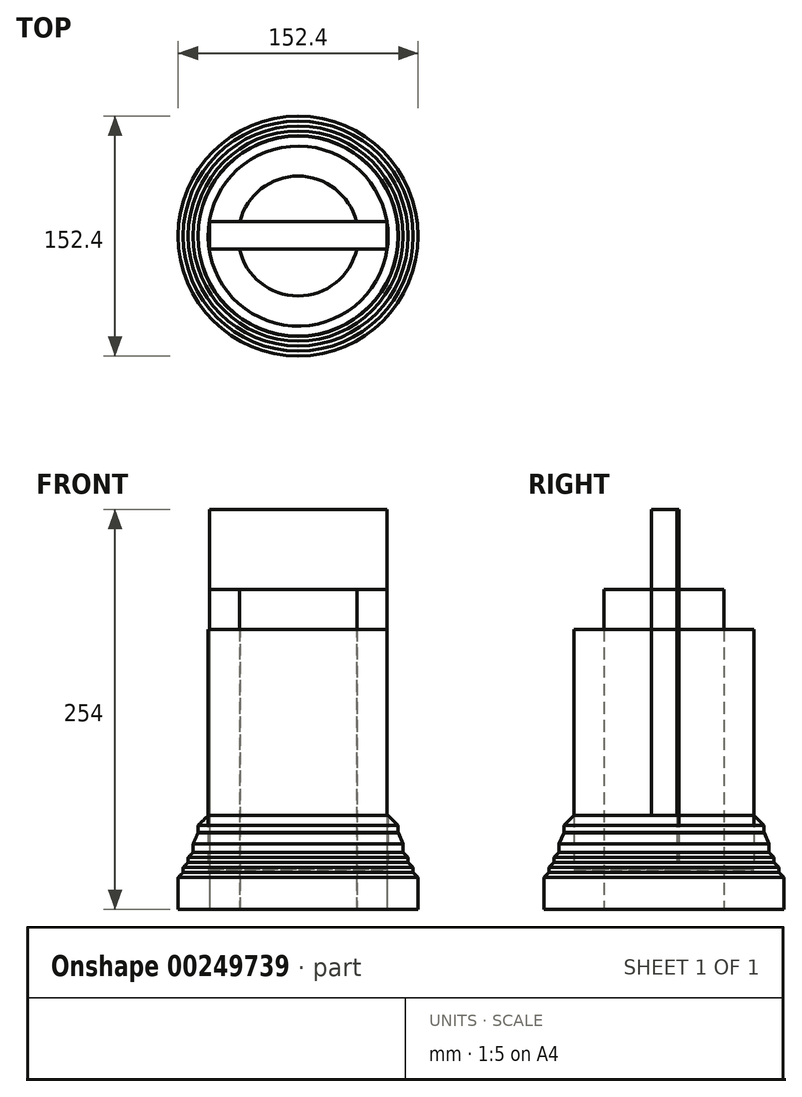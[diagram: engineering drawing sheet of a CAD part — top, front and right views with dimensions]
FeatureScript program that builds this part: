
annotation { "Feature Type Name" : "Feature", "Feature Type Description" : "" }
export const myFeature = defineFeature(function(context is Context, id is Id, definition is map)
    precondition{}
    {
        {
            var Q0;
            Q0=qCreatedBy(makeId("Top.planeOp"),FACE);
            var sketch = newSketch(context, id + "F0", { "sketchPlane" : qUnion([Q0])});
            skCircle(sketch, "E0", {"center": v(0, 0) * mm, "radius": 76.2 * mm});
            skCircle(sketch, "E1", {"center": v(0, 0) * mm, "radius": 57.15 * mm});
            skCircle(sketch, "E2", {"center": v(0, 0) * mm, "radius": 38.1 * mm});
            skLineSegment(sketch, "E3.bottom", {"start": v(-56.38, 9.32) * mm, "end": v(56.57, 9.32) * mm});
            skLineSegment(sketch, "E3.top", {"start": v(-56.38, -8.13) * mm, "end": v(56.57, -8.13) * mm});
            skLineSegment(sketch, "E3.left", {"start": v(-56.38, 9.32) * mm, "end": v(-56.38, -8.13) * mm});
            skLineSegment(sketch, "E3.right", {"start": v(56.57, 9.32) * mm, "end": v(56.57, -8.13) * mm});
            skCircle(sketch, "E4", {"center": v(0, 0) * mm, "radius": 73.03 * mm});
            skCircle(sketch, "E5", {"center": v(0, 0) * mm, "radius": 69.85 * mm});
            skCircle(sketch, "E6", {"center": v(0, 0) * mm, "radius": 66.68 * mm});
            skCircle(sketch, "E7", {"center": v(0, 0) * mm, "radius": 63.5 * mm});
            skSolve(sketch);
        }
        {
            var Q0;
            {var subQ0=sQuery(id+"F0.wireOp",EDGE,"E3.top");var subQ1=sQuery(id+"F0.wireOp",EDGE,"E2");var subQ2=makeQuery(id+"F0.imprint","INTERSECT",VERTEX,{"disambiguationData":[OD(0.0)],"derivedFrom":[subQ1,subQ0]});Q0=makeQuery(id+"F0.imprint","IMPRINT",FACE,{"disambiguationData":[TD([[makeQuery(id+"F0.imprint","IMPRINT",EDGE,{"disambiguationData":[TD([[subQ2,-1.0]])],"derivedFrom":subQ1}),1.0]])]});}
            var Q1;
            Q1=makeQuery(id+"F0.imprint","IMPRINT",FACE,{"disambiguationData":[TD([[makeQuery(id+"F0.imprint","IMPRINT",EDGE,{"derivedFrom":sQuery(id+"F0.wireOp",EDGE,"E0")}),1.0]])]});
            var Q2;
            {var subQ0=sQuery(id+"F0.wireOp",EDGE,"E3.bottom");var subQ1=sQuery(id+"F0.wireOp",EDGE,"E2");var subQ2=makeQuery(id+"F0.imprint","INTERSECT",VERTEX,{"disambiguationData":[OD(0.0)],"derivedFrom":[subQ1,subQ0]});Q2=makeQuery(id+"F0.imprint","IMPRINT",FACE,{"disambiguationData":[TD([[makeQuery(id+"F0.imprint","IMPRINT",EDGE,{"disambiguationData":[TD([[subQ2,-1.0]])],"derivedFrom":subQ1}),1.0]])]});}
            var Q3;
            Q3=makeQuery(id+"F0.imprint","IMPRINT",FACE,{"disambiguationData":[TD([[makeQuery(id+"F0.imprint","IMPRINT",EDGE,{"derivedFrom":sQuery(id+"F0.wireOp",EDGE,"E7")}),1.0]])]});
            var Q4;
            {var subQ5=sQuery(id+"F0.wireOp",EDGE,"E3.left");Q4=makeQuery(id+"F0.imprint","IMPRINT",FACE,{"disambiguationData":[TD([[makeQuery(id+"F0.imprint","IMPRINT",EDGE,{"derivedFrom":subQ5}),-1.0]])]});}
            var Q5;
            {var subQ0=sQuery(id+"F0.wireOp",EDGE,"E3.bottom");var subQ4=sQuery(id+"F0.wireOp",EDGE,"E2");var subQ5=makeQuery(id+"F0.imprint","INTERSECT",VERTEX,{"disambiguationData":[OD(0.0)],"derivedFrom":[subQ4,subQ0]});Q5=makeQuery(id+"F0.imprint","IMPRINT",FACE,{"disambiguationData":[TD([[makeQuery(id+"F0.imprint","IMPRINT",EDGE,{"disambiguationData":[TD([[subQ5,1.0]])],"derivedFrom":subQ4}),-1.0]])]});}
            var Q6;
            {var subQ5=sQuery(id+"F0.wireOp",EDGE,"E3.left");Q6=makeQuery(id+"F0.imprint","IMPRINT",FACE,{"disambiguationData":[TD([[makeQuery(id+"F0.imprint","IMPRINT",EDGE,{"derivedFrom":subQ5}),1.0]])]});}
            var Q7;
            Q7=makeQuery(id+"F0.imprint","IMPRINT",FACE,{"disambiguationData":[TD([[makeQuery(id+"F0.imprint","IMPRINT",EDGE,{"derivedFrom":sQuery(id+"F0.wireOp",EDGE,"E6")}),1.0]])]});
            var Q8;
            Q8=makeQuery(id+"F0.imprint","IMPRINT",FACE,{"disambiguationData":[TD([[makeQuery(id+"F0.imprint","IMPRINT",EDGE,{"derivedFrom":sQuery(id+"F0.wireOp",EDGE,"E5")}),1.0]])]});
            var Q9;
            {var subQ0=sQuery(id+"F0.wireOp",EDGE,"E3.bottom");var subQ1=sQuery(id+"F0.wireOp",EDGE,"E2");var subQ2=makeQuery(id+"F0.imprint","INTERSECT",VERTEX,{"disambiguationData":[OD(0.0)],"derivedFrom":[subQ1,subQ0]});Q9=makeQuery(id+"F0.imprint","IMPRINT",FACE,{"disambiguationData":[TD([[makeQuery(id+"F0.imprint","IMPRINT",EDGE,{"disambiguationData":[TD([[subQ2,1.0]])],"derivedFrom":subQ1}),1.0]])]});}
            var Q10;
            Q10=makeQuery(id+"F0.imprint","IMPRINT",FACE,{"disambiguationData":[TD([[makeQuery(id+"F0.imprint","IMPRINT",EDGE,{"derivedFrom":sQuery(id+"F0.wireOp",EDGE,"E4")}),1.0]])]});
            var Q11;
            {var subQ2=sQuery(id+"F0.wireOp",EDGE,"E1");var subQ6=sQuery(id+"F0.wireOp",EDGE,"E3.bottom");var subQ7=makeQuery(id+"F0.imprint","INTERSECT",VERTEX,{"derivedFrom":[subQ2,subQ6]});Q11=makeQuery(id+"F0.imprint","IMPRINT",FACE,{"disambiguationData":[TD([[makeQuery(id+"F0.imprint","IMPRINT",EDGE,{"disambiguationData":[TD([[subQ7,1.0]])],"derivedFrom":subQ2}),1.0]])]});}
            var Q12;
            {var subQ0=sQuery(id+"F0.wireOp",EDGE,"E3.right");var subQ1=sQuery(id+"F0.wireOp",EDGE,"E1");var subQ3=makeQuery(id+"F0.imprint","INTERSECT",VERTEX,{"derivedFrom":[subQ1,subQ0]});Q12=makeQuery(id+"F0.imprint","IMPRINT",FACE,{"disambiguationData":[TD([[makeQuery(id+"F0.imprint","IMPRINT",EDGE,{"disambiguationData":[TD([[subQ3,1.0]])],"derivedFrom":subQ1}),1.0]])]});}
            var Q13;
            {var subQ0=sQuery(id+"F0.wireOp",EDGE,"E3.bottom");var subQ1=sQuery(id+"F0.wireOp",EDGE,"E1");var subQ2=makeQuery(id+"F0.imprint","INTERSECT",VERTEX,{"derivedFrom":[subQ1,subQ0]});Q13=makeQuery(id+"F0.imprint","IMPRINT",FACE,{"disambiguationData":[TD([[makeQuery(id+"F0.imprint","IMPRINT",EDGE,{"disambiguationData":[TD([[subQ2,1.0]])],"derivedFrom":subQ1}),-1.0]])]});}
            extrude(context, id + "F1", {"entities" : qUnion([Q0, Q1, Q2, Q3, Q4, Q5, Q6, Q7, Q8, Q9, Q10, Q11, Q12, Q13]), "depth" : 25.4 * mm});
        }
        {
            var Q0;
            Q0=makeQuery(id+"F0.imprint","IMPRINT",FACE,{"disambiguationData":[TD([[makeQuery(id+"F0.imprint","IMPRINT",EDGE,{"derivedFrom":sQuery(id+"F0.wireOp",EDGE,"E4")}),1.0]])]});
            extrude(context, id + "F2", {"entities" : qUnion([Q0]), "operationType" : NewBodyOperationType.ADD, "depth" : 31.75 * mm});
        }
        {
            var Q0;
            Q0=makeQuery(id+"F0.imprint","IMPRINT",FACE,{"disambiguationData":[TD([[makeQuery(id+"F0.imprint","IMPRINT",EDGE,{"derivedFrom":sQuery(id+"F0.wireOp",EDGE,"E5")}),1.0]])]});
            extrude(context, id + "F3", {"entities" : qUnion([Q0]), "operationType" : NewBodyOperationType.ADD, "depth" : 38.1 * mm});
        }
        {
            var Q0;
            Q0=makeQuery(id+"F0.imprint","IMPRINT",FACE,{"disambiguationData":[TD([[makeQuery(id+"F0.imprint","IMPRINT",EDGE,{"derivedFrom":sQuery(id+"F0.wireOp",EDGE,"E6")}),1.0]])]});
            extrude(context, id + "F4", {"entities" : qUnion([Q0]), "operationType" : NewBodyOperationType.ADD, "depth" : 50.8 * mm});
        }
        {
            var Q0;
            Q0=makeQuery(id+"F0.imprint","IMPRINT",FACE,{"disambiguationData":[TD([[makeQuery(id+"F0.imprint","IMPRINT",EDGE,{"derivedFrom":sQuery(id+"F0.wireOp",EDGE,"E7")}),1.0]])]});
            extrude(context, id + "F5", {"entities" : qUnion([Q0]), "operationType" : NewBodyOperationType.ADD, "depth" : 63.5 * mm});
        }
        {
            var Q0;
            {var subQ0=sQuery(id+"F0.wireOp",EDGE,"E3.bottom");var subQ4=sQuery(id+"F0.wireOp",EDGE,"E2");var subQ5=makeQuery(id+"F0.imprint","INTERSECT",VERTEX,{"disambiguationData":[OD(0.0)],"derivedFrom":[subQ4,subQ0]});Q0=makeQuery(id+"F0.imprint","IMPRINT",FACE,{"disambiguationData":[TD([[makeQuery(id+"F0.imprint","IMPRINT",EDGE,{"disambiguationData":[TD([[subQ5,1.0]])],"derivedFrom":subQ4}),-1.0]])]});}
            var Q1;
            {var subQ2=sQuery(id+"F0.wireOp",EDGE,"E1");var subQ6=sQuery(id+"F0.wireOp",EDGE,"E3.bottom");var subQ7=makeQuery(id+"F0.imprint","INTERSECT",VERTEX,{"derivedFrom":[subQ2,subQ6]});Q1=makeQuery(id+"F0.imprint","IMPRINT",FACE,{"disambiguationData":[TD([[makeQuery(id+"F0.imprint","IMPRINT",EDGE,{"disambiguationData":[TD([[subQ7,1.0]])],"derivedFrom":subQ2}),1.0]])]});}
            var Q2;
            {var subQ5=sQuery(id+"F0.wireOp",EDGE,"E3.left");Q2=makeQuery(id+"F0.imprint","IMPRINT",FACE,{"disambiguationData":[TD([[makeQuery(id+"F0.imprint","IMPRINT",EDGE,{"derivedFrom":subQ5}),-1.0]])]});}
            var Q3;
            {var subQ0=sQuery(id+"F0.wireOp",EDGE,"E3.top");var subQ1=sQuery(id+"F0.wireOp",EDGE,"E2");var subQ2=makeQuery(id+"F0.imprint","INTERSECT",VERTEX,{"disambiguationData":[OD(0.0)],"derivedFrom":[subQ1,subQ0]});Q3=makeQuery(id+"F0.imprint","IMPRINT",FACE,{"disambiguationData":[TD([[makeQuery(id+"F0.imprint","IMPRINT",EDGE,{"disambiguationData":[TD([[subQ2,-1.0]])],"derivedFrom":subQ1}),1.0]])]});}
            var Q4;
            {var subQ0=sQuery(id+"F0.wireOp",EDGE,"E3.bottom");var subQ1=sQuery(id+"F0.wireOp",EDGE,"E2");var subQ2=makeQuery(id+"F0.imprint","INTERSECT",VERTEX,{"disambiguationData":[OD(0.0)],"derivedFrom":[subQ1,subQ0]});Q4=makeQuery(id+"F0.imprint","IMPRINT",FACE,{"disambiguationData":[TD([[makeQuery(id+"F0.imprint","IMPRINT",EDGE,{"disambiguationData":[TD([[subQ2,1.0]])],"derivedFrom":subQ1}),1.0]])]});}
            var Q5;
            {var subQ0=sQuery(id+"F0.wireOp",EDGE,"E3.bottom");var subQ1=sQuery(id+"F0.wireOp",EDGE,"E2");var subQ2=makeQuery(id+"F0.imprint","INTERSECT",VERTEX,{"disambiguationData":[OD(0.0)],"derivedFrom":[subQ1,subQ0]});Q5=makeQuery(id+"F0.imprint","IMPRINT",FACE,{"disambiguationData":[TD([[makeQuery(id+"F0.imprint","IMPRINT",EDGE,{"disambiguationData":[TD([[subQ2,-1.0]])],"derivedFrom":subQ1}),1.0]])]});}
            var Q6;
            {var subQ5=sQuery(id+"F0.wireOp",EDGE,"E3.left");Q6=makeQuery(id+"F0.imprint","IMPRINT",FACE,{"disambiguationData":[TD([[makeQuery(id+"F0.imprint","IMPRINT",EDGE,{"derivedFrom":subQ5}),1.0]])]});}
            extrude(context, id + "F6", {"entities" : qUnion([Q0, Q1, Q2, Q3, Q4, Q5, Q6]), "operationType" : NewBodyOperationType.ADD, "depth" : 25.4 * mm});
        }
        {
            var Q0;
            {var subQ0=sQuery(id+"F0.wireOp",EDGE,"E3.bottom");var subQ4=sQuery(id+"F0.wireOp",EDGE,"E2");var subQ5=makeQuery(id+"F0.imprint","INTERSECT",VERTEX,{"disambiguationData":[OD(0.0)],"derivedFrom":[subQ4,subQ0]});Q0=makeQuery(id+"F0.imprint","IMPRINT",FACE,{"disambiguationData":[TD([[makeQuery(id+"F0.imprint","IMPRINT",EDGE,{"disambiguationData":[TD([[subQ5,1.0]])],"derivedFrom":subQ4}),-1.0]])]});}
            var Q1;
            {var subQ2=sQuery(id+"F0.wireOp",EDGE,"E1");var subQ6=sQuery(id+"F0.wireOp",EDGE,"E3.bottom");var subQ7=makeQuery(id+"F0.imprint","INTERSECT",VERTEX,{"derivedFrom":[subQ2,subQ6]});Q1=makeQuery(id+"F0.imprint","IMPRINT",FACE,{"disambiguationData":[TD([[makeQuery(id+"F0.imprint","IMPRINT",EDGE,{"disambiguationData":[TD([[subQ7,1.0]])],"derivedFrom":subQ2}),1.0]])]});}
            var Q2;
            {var subQ5=sQuery(id+"F0.wireOp",EDGE,"E3.left");Q2=makeQuery(id+"F0.imprint","IMPRINT",FACE,{"disambiguationData":[TD([[makeQuery(id+"F0.imprint","IMPRINT",EDGE,{"derivedFrom":subQ5}),-1.0]])]});}
            var Q3;
            {var subQ5=sQuery(id+"F0.wireOp",EDGE,"E3.left");Q3=makeQuery(id+"F0.imprint","IMPRINT",FACE,{"disambiguationData":[TD([[makeQuery(id+"F0.imprint","IMPRINT",EDGE,{"derivedFrom":subQ5}),1.0]])]});}
            var Q4;
            {var subQ0=sQuery(id+"F0.wireOp",EDGE,"E3.bottom");var subQ1=sQuery(id+"F0.wireOp",EDGE,"E2");var subQ2=makeQuery(id+"F0.imprint","INTERSECT",VERTEX,{"disambiguationData":[OD(0.0)],"derivedFrom":[subQ1,subQ0]});Q4=makeQuery(id+"F0.imprint","IMPRINT",FACE,{"disambiguationData":[TD([[makeQuery(id+"F0.imprint","IMPRINT",EDGE,{"disambiguationData":[TD([[subQ2,-1.0]])],"derivedFrom":subQ1}),1.0]])]});}
            var Q5;
            {var subQ0=sQuery(id+"F0.wireOp",EDGE,"E3.top");var subQ1=sQuery(id+"F0.wireOp",EDGE,"E2");var subQ2=makeQuery(id+"F0.imprint","INTERSECT",VERTEX,{"disambiguationData":[OD(0.0)],"derivedFrom":[subQ1,subQ0]});Q5=makeQuery(id+"F0.imprint","IMPRINT",FACE,{"disambiguationData":[TD([[makeQuery(id+"F0.imprint","IMPRINT",EDGE,{"disambiguationData":[TD([[subQ2,-1.0]])],"derivedFrom":subQ1}),1.0]])]});}
            var Q6;
            {var subQ0=sQuery(id+"F0.wireOp",EDGE,"E3.bottom");var subQ1=sQuery(id+"F0.wireOp",EDGE,"E2");var subQ2=makeQuery(id+"F0.imprint","INTERSECT",VERTEX,{"disambiguationData":[OD(0.0)],"derivedFrom":[subQ1,subQ0]});Q6=makeQuery(id+"F0.imprint","IMPRINT",FACE,{"disambiguationData":[TD([[makeQuery(id+"F0.imprint","IMPRINT",EDGE,{"disambiguationData":[TD([[subQ2,1.0]])],"derivedFrom":subQ1}),1.0]])]});}
            extrude(context, id + "F7", {"entities" : qUnion([Q0, Q1, Q2, Q3, Q4, Q5, Q6]), "depth" : 177.8 * mm});
        }
        {
            var Q0;
            {var subQ0=sQuery(id+"F0.wireOp",EDGE,"E3.top");var subQ1=sQuery(id+"F0.wireOp",EDGE,"E2");var subQ2=makeQuery(id+"F0.imprint","INTERSECT",VERTEX,{"disambiguationData":[OD(0.0)],"derivedFrom":[subQ1,subQ0]});Q0=makeQuery(id+"F0.imprint","IMPRINT",FACE,{"disambiguationData":[TD([[makeQuery(id+"F0.imprint","IMPRINT",EDGE,{"disambiguationData":[TD([[subQ2,-1.0]])],"derivedFrom":subQ1}),1.0]])]});}
            var Q1;
            {var subQ0=sQuery(id+"F0.wireOp",EDGE,"E3.bottom");var subQ1=sQuery(id+"F0.wireOp",EDGE,"E2");var subQ2=makeQuery(id+"F0.imprint","INTERSECT",VERTEX,{"disambiguationData":[OD(0.0)],"derivedFrom":[subQ1,subQ0]});Q1=makeQuery(id+"F0.imprint","IMPRINT",FACE,{"disambiguationData":[TD([[makeQuery(id+"F0.imprint","IMPRINT",EDGE,{"disambiguationData":[TD([[subQ2,1.0]])],"derivedFrom":subQ1}),1.0]])]});}
            var Q2;
            {var subQ5=sQuery(id+"F0.wireOp",EDGE,"E3.left");Q2=makeQuery(id+"F0.imprint","IMPRINT",FACE,{"disambiguationData":[TD([[makeQuery(id+"F0.imprint","IMPRINT",EDGE,{"derivedFrom":subQ5}),1.0]])]});}
            var Q3;
            {var subQ2=sQuery(id+"F0.wireOp",EDGE,"E1");var subQ6=sQuery(id+"F0.wireOp",EDGE,"E3.bottom");var subQ7=makeQuery(id+"F0.imprint","INTERSECT",VERTEX,{"derivedFrom":[subQ2,subQ6]});Q3=makeQuery(id+"F0.imprint","IMPRINT",FACE,{"disambiguationData":[TD([[makeQuery(id+"F0.imprint","IMPRINT",EDGE,{"disambiguationData":[TD([[subQ7,1.0]])],"derivedFrom":subQ2}),1.0]])]});}
            var Q4;
            {var subQ0=sQuery(id+"F0.wireOp",EDGE,"E3.bottom");var subQ1=sQuery(id+"F0.wireOp",EDGE,"E2");var subQ2=makeQuery(id+"F0.imprint","INTERSECT",VERTEX,{"disambiguationData":[OD(0.0)],"derivedFrom":[subQ1,subQ0]});Q4=makeQuery(id+"F0.imprint","IMPRINT",FACE,{"disambiguationData":[TD([[makeQuery(id+"F0.imprint","IMPRINT",EDGE,{"disambiguationData":[TD([[subQ2,-1.0]])],"derivedFrom":subQ1}),1.0]])]});}
            extrude(context, id + "F8", {"entities" : qUnion([Q0, Q1, Q2, Q3, Q4]), "depth" : 203.2 * mm});
        }
        {
            var Q0;
            {var subQ5=sQuery(id+"F0.wireOp",EDGE,"E3.left");Q0=makeQuery(id+"F0.imprint","IMPRINT",FACE,{"disambiguationData":[TD([[makeQuery(id+"F0.imprint","IMPRINT",EDGE,{"derivedFrom":subQ5}),1.0]])]});}
            var Q1;
            {var subQ0=sQuery(id+"F0.wireOp",EDGE,"E3.bottom");var subQ1=sQuery(id+"F0.wireOp",EDGE,"E2");var subQ2=makeQuery(id+"F0.imprint","INTERSECT",VERTEX,{"disambiguationData":[OD(0.0)],"derivedFrom":[subQ1,subQ0]});Q1=makeQuery(id+"F0.imprint","IMPRINT",FACE,{"disambiguationData":[TD([[makeQuery(id+"F0.imprint","IMPRINT",EDGE,{"disambiguationData":[TD([[subQ2,-1.0]])],"derivedFrom":subQ1}),1.0]])]});}
            var Q2;
            {var subQ2=sQuery(id+"F0.wireOp",EDGE,"E1");var subQ6=sQuery(id+"F0.wireOp",EDGE,"E3.bottom");var subQ7=makeQuery(id+"F0.imprint","INTERSECT",VERTEX,{"derivedFrom":[subQ2,subQ6]});Q2=makeQuery(id+"F0.imprint","IMPRINT",FACE,{"disambiguationData":[TD([[makeQuery(id+"F0.imprint","IMPRINT",EDGE,{"disambiguationData":[TD([[subQ7,1.0]])],"derivedFrom":subQ2}),1.0]])]});}
            extrude(context, id + "F9", {"entities" : qUnion([Q0, Q1, Q2]), "depth" : 254 * mm});
        }
        {
            var Q0;
            Q0=makeQuery(id+"F1.opExtrude","CAP_EDGE",EDGE,{"disambiguationData":[OSD([sQuery(id+"F0.wireOp",EDGE,"E0")])],"isStart":false});
            var Q1;
            Q1=makeQuery(id+"F2.opExtrude","CAP_EDGE",EDGE,{"disambiguationData":[OSD([sQuery(id+"F0.wireOp",EDGE,"E4")])],"isStart":false});
            var Q2;
            Q2=makeQuery(id+"F3.opExtrude","CAP_EDGE",EDGE,{"disambiguationData":[OSD([sQuery(id+"F0.wireOp",EDGE,"E5")])],"isStart":false});
            var Q3;
            Q3=makeQuery(id+"F4.opExtrude","CAP_EDGE",EDGE,{"disambiguationData":[OSD([sQuery(id+"F0.wireOp",EDGE,"E6")])],"isStart":false});
            chamfer(context, id + "F10", {"entities" : qUnion([Q0, Q1, Q2, Q3]), "width" : 5.08 * mm, "tangentPropagation" : true});
        }
        {
            var Q0;
            Q0=makeQuery(id+"F5.opExtrude","CAP_EDGE",EDGE,{"disambiguationData":[OSD([sQuery(id+"F0.wireOp",EDGE,"E7")])],"isStart":false});
            chamfer(context, id + "F11", {"entities" : qUnion([Q0]), "width" : 10.16 * mm, "tangentPropagation" : true});
        }
        {
            var Q0;
            {var subQ0=sQuery(id+"F0.wireOp",EDGE,"E6");Q0=makeQuery(id+"F10.opChamfer","BLEND_EDGE",EDGE,{"blendedFrom":[makeQuery(id+"F4.opExtrude","CAP_EDGE",EDGE,{"disambiguationData":[OSD([subQ0])],"isStart":false}),makeQuery(id+"F4.opExtrude","SWEPT_FACE",FACE,{"disambiguationData":[OSD([subQ0])]})],"blendedInto":[makeQuery(id+"F4.opExtrude","SWEPT_FACE",FACE,{"disambiguationData":[OSD([subQ0])]})]});}
            chamfer(context, id + "F12", {"entities" : qUnion([Q0]), "width" : 10.16 * mm, "tangentPropagation" : true});
        }
    });
